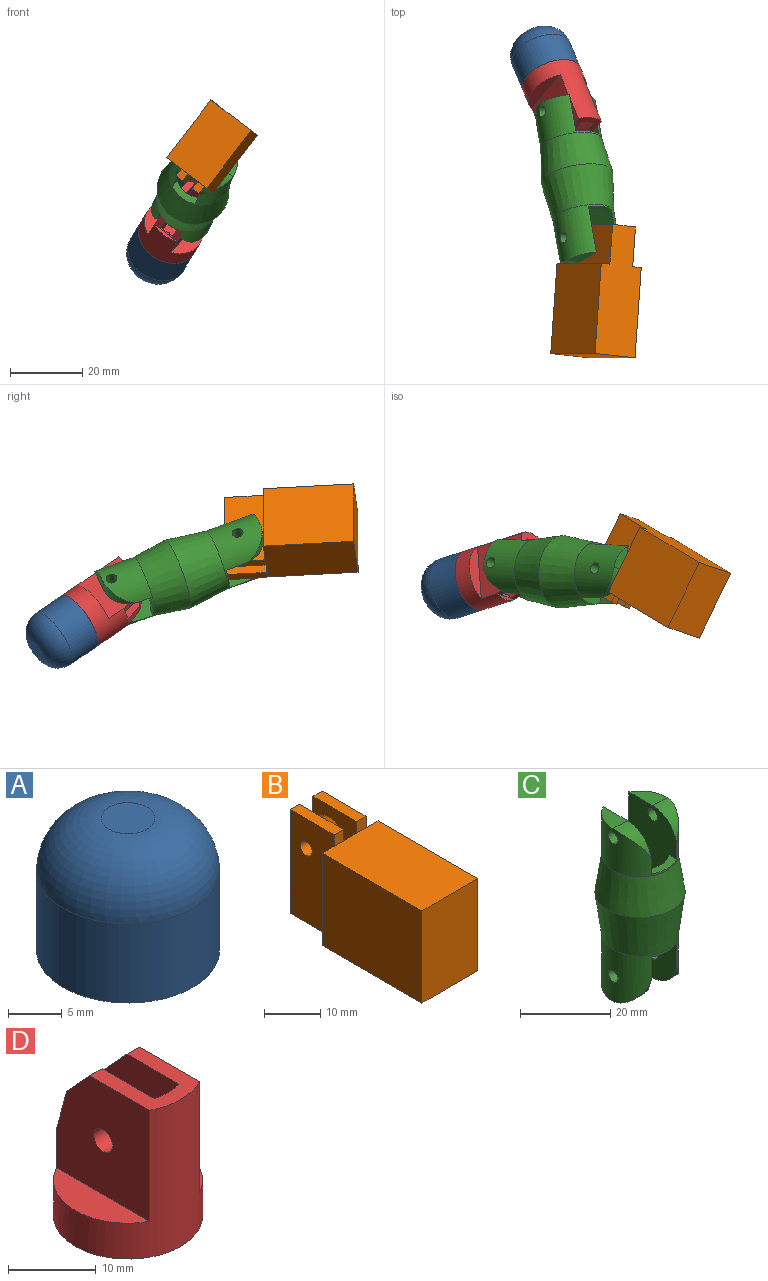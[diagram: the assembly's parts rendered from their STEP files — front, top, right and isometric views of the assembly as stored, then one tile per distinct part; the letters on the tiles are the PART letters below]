
ASSEMBLY  parts=4 mates=3
PART A: 7 faces, bbox 17x17x15 mm
  f0: cylinder r=8.5mm len=17mm, axis (0,0,-1), area 480.7mm2, adj f2,f3
  f1: plane 5x5mm, normal (0,0,1), area 19.6mm2, adj f3
  f2: plane 17x17mm, normal (0,0,-1), area 113.9mm2, adj f0,f4
  f3: torus R=2.5mm, axis (0,0,1), area 374.2mm2, adj f0,f1
  f4: cylinder r=6mm len=12mm, axis (0,0,-1), area 339.3mm2, adj f2,f6
  f5: plane 5x5mm, normal (0,0,-1), area 19.6mm2, adj f6
  f6: torus R=2.5mm, axis (0,0,1), area 163.3mm2, adj f4,f5
PART B: 22 faces, bbox 14x36x22.5 mm
  f0: plane 2.5x2.3mm, normal (0,-1,0), area 5.7mm2, adj f3,f4,f5,f13
  f1: plane 2.5x2.3mm, normal (0,-1,0), area 5.7mm2, adj f8,f9,f10,f13
  f2: plane 11x3.4mm, normal (0,0,1), area 37.4mm2, adj f3,f7,f8,f12
  f3: plane 12.7x11mm, normal (1,0,0), area 89.4mm2, adj f0,f2,f4,f7,f12,f20
  f4: plane 11x2.3mm, normal (0,0,1), area 25.3mm2, adj f0,f3,f5,f7
  f5: plane 22.5x11mm, normal (-1,0,0), area 240.4mm2, adj f0,f4,f6,f7,f17,f18
  f6: plane 36x14mm, normal (0,0,-1), area 438mm2, adj f5,f7,f10,f11,f14,f15,f16,f17
  f7: plane 22.5x8mm, normal (0,1,0), area 136.8mm2, adj f2,f3,f4,f5,f6,f8,f9,f10
  f8: plane 12.7x11mm, normal (-1,0,0), area 89.4mm2, adj f1,f2,f7,f9,f12,f21
  f9: plane 11x2.3mm, normal (0,0,1), area 25.3mm2, adj f1,f7,f8,f10
  f10: plane 22.5x11mm, normal (1,0,0), area 240.4mm2, adj f1,f6,f7,f9,f11,f18
  f11: plane 20x3mm, normal (0,1,0), area 60mm2, adj f6,f10,f13,f15
  f12: plane 10.2x3.4mm, normal (0,1,0), area 34.7mm2, adj f2,f3,f8,f13
  f13: plane 25x14mm, normal (0,0,1), area 350mm2, adj f0,f1,f11,f12,f14,f15,f16,f17
  f14: plane 25x20mm, normal (-1,0,0), area 500mm2, adj f6,f13,f16,f17
  f15: plane 25x20mm, normal (1,0,0), area 500mm2, adj f6,f11,f13,f16
  f16: plane 20x14mm, normal (0,-1,0), area 280mm2, adj f6,f13,f14,f15
  f17: plane 20x3mm, normal (0,1,0), area 60mm2, adj f5,f6,f13,f14
  f18: cylinder r=1.5mm len=8mm, axis (1,0,0), area 75.4mm2, adj f5,f10
  f19: cylinder r=2.5mm len=5mm, axis (1,0,0), area 6.3mm2, adj f20,f21
  f20: cone r=2.5mm half-angle=45deg, axis (-1,0,0), area 43.3mm2, adj f3,f19
  f21: cone r=2.5mm half-angle=45deg, axis (1,0,0), area 43.3mm2, adj f8,f19
PART C: 30 faces, bbox 20x20x46.8 mm
  f0: cylinder r=8.5mm len=17mm, axis (0,0,-1), area 373.2mm2, adj f1,f2,f4,f12,f13,f21,f23,f26
  f1: plane 46.8x15mm, normal (-1,0,0), area 555.1mm2, adj f0,f3,f5,f6,f7,f9,f10,f13
  f2: plane 46.8x15mm, normal (1,0,0), area 555.1mm2, adj f0,f3,f4,f5,f6,f7,f8,f9
  f3: cylinder r=6.5mm len=8mm, axis (0,0,-1), area 5.6mm2, adj f1,f2,f15,f27
  f4: plane 7.5x4.5mm, normal (0,0,1), area 24mm2, adj f0,f2,f28
  f5: cylinder r=6.5mm len=8mm, axis (0,0,-1), area 5.6mm2, adj f1,f2,f15,f26
  f6: cylinder r=8.5mm len=17mm, axis (0,0,-1), area 467.9mm2, adj f1,f2,f8,f10,f11,f16,f17,f20
  f7: cylinder r=6.5mm len=8mm, axis (0,0,-1), area 5.4mm2, adj f1,f2,f14,f16
  f8: plane 7x4.49mm, normal (0,0,-1), area 21.8mm2, adj f2,f6,f24
  f9: cylinder r=6.5mm len=8mm, axis (0,0,-1), area 5.4mm2, adj f1,f2,f14,f17
  f10: plane 7x4.49mm, normal (0,0,-1), area 21.8mm2, adj f1,f6,f25
  f11: cone r=8.5mm half-angle=7.4deg, axis (0,0,1), area 674mm2, adj f6,f12
  f12: cone r=10mm half-angle=8.5deg, axis (0,0,-1), area 587.7mm2, adj f0,f11
  f13: plane 7.5x4.5mm, normal (0,0,1), area 24mm2, adj f0,f1,f29
  f14: cone r=6.52mm half-angle=7.4deg, axis (0,0,1), area 520.7mm2, adj f7,f9,f15,f18,f19
  f15: cone r=8.02mm half-angle=8.5deg, axis (0,0,-1), area 454mm2, adj f3,f5,f14,f18,f19
  f16: plane 8x3.38mm, normal (0,0,-1), area 16.9mm2, adj f1,f2,f6,f7
  f17: plane 8x3.38mm, normal (0,0,-1), area 16.9mm2, adj f1,f2,f6,f9
  f18: cylinder r=6.5mm len=21.22mm, axis (0,0,-1), area 250.5mm2, adj f2,f14,f15
  f19: cylinder r=6.5mm len=21.22mm, axis (0,0,-1), area 250.5mm2, adj f1,f14,f15
  f20: cylinder r=1.5mm len=4.5mm, axis (1,0,0), area 41.8mm2, adj f2,f6
  f21: cylinder r=1.5mm len=4.5mm, axis (1,0,0), area 41.8mm2, adj f0,f2
  f22: cylinder r=1.5mm len=4.5mm, axis (1,0,0), area 41.8mm2, adj f1,f6
  f23: cylinder r=1.5mm len=4.5mm, axis (1,0,0), area 41.8mm2, adj f0,f1
  f24: cylinder r=8mm len=8mm, axis (-1,0,0), area 31.7mm2, adj f2,f6,f8
  f25: cylinder r=8mm len=8mm, axis (-1,0,0), area 31.7mm2, adj f1,f6,f10
  f26: plane 8x3.38mm, normal (0,0,1), area 16.9mm2, adj f0,f1,f2,f5
  f27: plane 8x3.38mm, normal (0,0,1), area 16.9mm2, adj f0,f1,f2,f3
  f28: cylinder r=7.5mm len=7.5mm, axis (-1,0,0), area 28.9mm2, adj f0,f2,f4
  f29: cylinder r=7.5mm len=7.5mm, axis (-1,0,0), area 28.9mm2, adj f0,f1,f13
PART D: 24 faces, bbox 17x17x20.5 mm
  f0: cylinder r=6.5mm len=4.79mm, axis (0,0,1), area 19.2mm2, adj f9,f10,f12,f17
  f1: plane 8x1mm, normal (0,0,1), area 5.4mm2, adj f2,f13,f16,f17
  f2: cylinder r=8.5mm len=20.5mm, axis (0,0,-1), area 442mm2, adj f1,f3,f4,f5,f6,f7,f8
  f3: plane 10.67x8mm, normal (0,0,1), area 48.5mm2, adj f2,f6,f8,f9,f10,f11,f14,f15
  f4: plane 17x17mm, normal (0,0,-1), area 223.4mm2, adj f2,f21,f22
  f5: plane 15x4.5mm, normal (0,0,1), area 48.1mm2, adj f2,f6
  f6: plane 15.5x15mm, normal (1,0,0), area 206.5mm2, adj f2,f3,f5,f15,f16,f23
  f7: plane 15x4.5mm, normal (0,0,1), area 48.1mm2, adj f2,f8
  f8: plane 15.5x15mm, normal (-1,0,0), area 206.5mm2, adj f2,f3,f7,f13,f14,f23
  f9: plane 15.5x13.68mm, normal (-1,0,0), area 148.1mm2, adj f0,f3,f11,f12,f15,f16,f17,f19
  f10: plane 15.5x13.68mm, normal (1,0,0), area 148.1mm2, adj f0,f3,f11,f12,f13,f14,f17,f18
  f11: cylinder r=6.5mm len=15.5mm, axis (0,0,1), area 63mm2, adj f3,f9,f10,f12
  f12: plane 13x4mm, normal (0,0,1), area 47.6mm2, adj f0,f9,f10,f11,f21,f22
  f13: plane 5.91x2mm, normal (0,0.97,0.26), area 12.2mm2, adj f1,f8,f10,f14
  f14: plane 4.09x3.73mm, normal (0,0.74,0.67), area 11.1mm2, adj f3,f8,f10,f13
  f15: plane 4.09x3.73mm, normal (0,0.74,0.67), area 11.1mm2, adj f3,f6,f9,f16
  f16: plane 5.91x2mm, normal (0,0.97,0.26), area 12.2mm2, adj f1,f6,f9,f15
  f17: plane 4x1.32mm, normal (0,-0.58,0.82), area 5.4mm2, adj f0,f1,f9,f10
  f18: cone r=3.5mm half-angle=45deg, axis (-1,0,0), area 36.7mm2, adj f10,f20
  f19: cone r=3.5mm half-angle=45deg, axis (1,0,0), area 36.7mm2, adj f9,f20
  f20: cylinder r=2mm len=4mm, axis (1,0,0), area 12.6mm2, adj f18,f19
  f21: cylinder r=0.75mm len=5mm, axis (0,0,-1), area 23.6mm2, adj f4,f12
  f22: cylinder r=0.75mm len=5mm, axis (0,0,-1), area 23.6mm2, adj f4,f12
  f23: cylinder r=1.5mm len=8mm, axis (-1,0,0), area 75.4mm2, adj f6,f8
PLACE A rot(axis=(-0.94,0.19,0.3),133deg) t=(8.05,-51.68,32.82)mm
PLACE B rot(axis=(-0.04,-1,0.01),142.4deg) t=(-4.5,-14.25,11.16)mm fixed
PLACE C rot(axis=(-0.22,-0.81,-0.54),151.9deg) t=(-13.48,-24.54,0.99)mm
PLACE D rot(axis=(0.28,-0.4,0.87),159.6deg) t=(-39.73,62.85,-45.61)mm
MATE revolute D.f23 <-> C.f21  axis (0.79,-0.09,-0.61) through (-17.27,16.24,-16.36)mm
MATE revolute C.f20 <-> B.f18  axis (0.79,-0.09,-0.61) through (-17.7,-17.88,1.13)mm
MATE fastened D.f2 <-> A.f0  axis (-0.33,0.78,-0.53) through (-24.49,26.34,-20.61)mm
